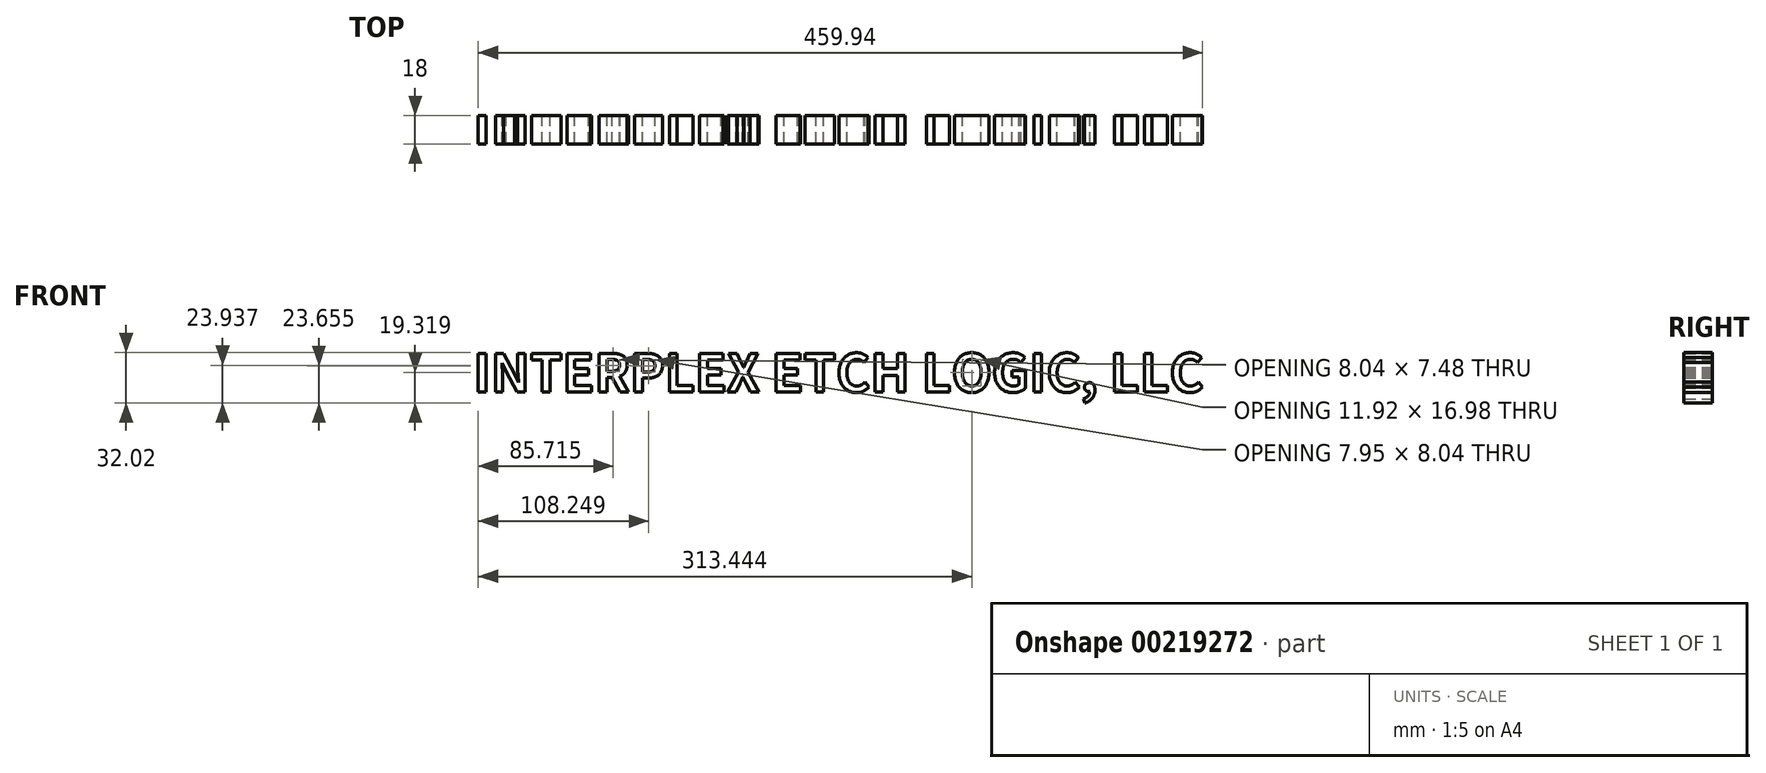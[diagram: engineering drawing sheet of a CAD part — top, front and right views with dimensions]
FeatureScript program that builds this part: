
annotation { "Feature Type Name" : "Feature", "Feature Type Description" : "" }
export const myFeature = defineFeature(function(context is Context, id is Id, definition is map)
    precondition{}
    {
        {
            var Q0;
            Q0=qCreatedBy(makeId("Front.planeOp"),FACE);
            var sketch = newSketch(context, id + "F0", { "sketchPlane" : qUnion([Q0])});
            skText(sketch, "E0", { "text": "INTERPLEX ETCH LOGIC, LLC", "fontName": "NotoSansCJKsc-Bold.otf"});
            const initialGuessF0  = {"E0": [-0.05261, -0.01415, 1, 0, 0.02384]};
            skSetInitialGuess(sketch, initialGuessF0);
            skSolve(sketch);
        }
        {
            var Q0;
            Q0 = qSketchRegion(id + "F0", true);
            extrude(context, id + "F1", {"entities" : qUnion([Q0]), "depth" : 18 * mm});
        }
    });
